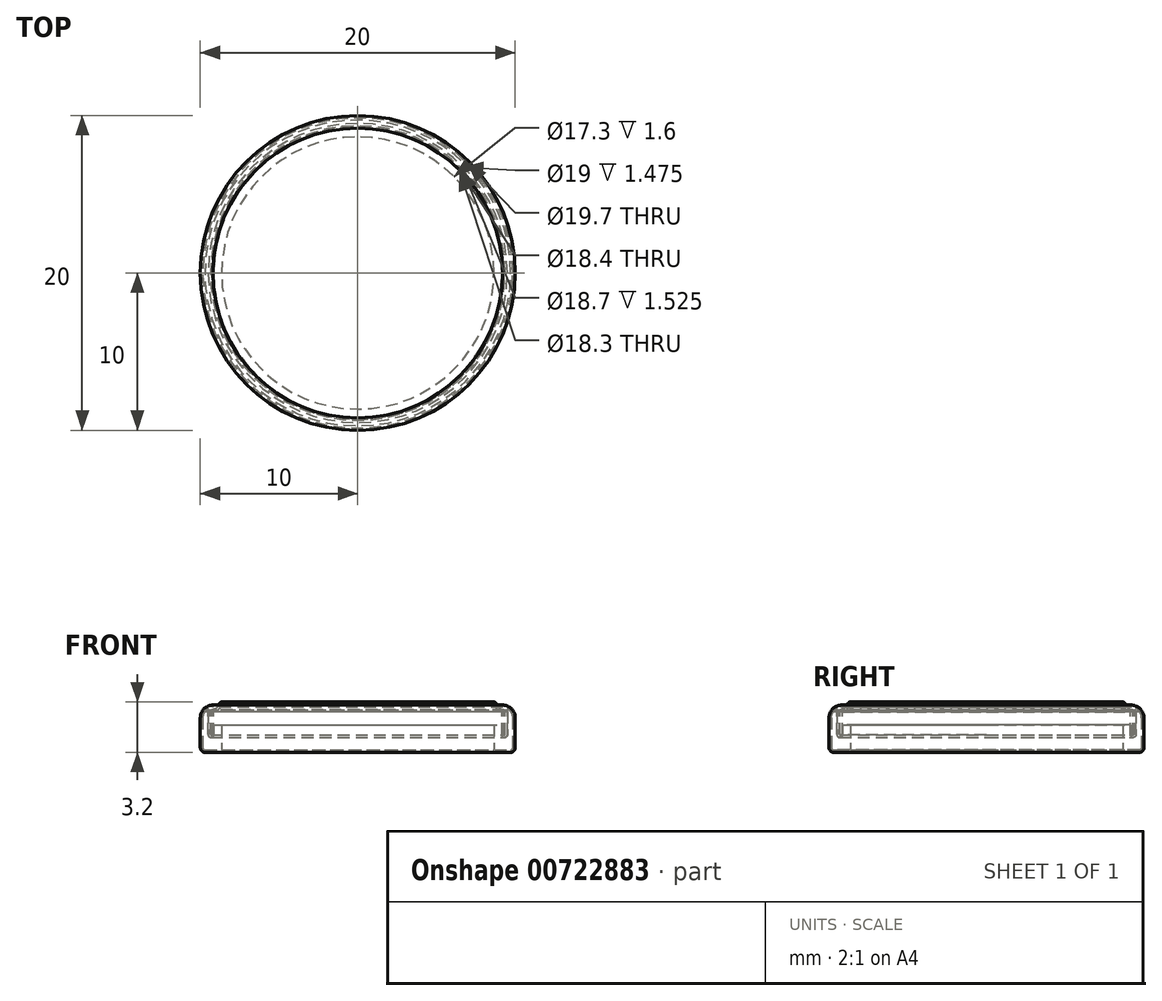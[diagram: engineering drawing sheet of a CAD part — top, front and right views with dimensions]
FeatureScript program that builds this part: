
annotation { "Feature Type Name" : "Feature", "Feature Type Description" : "" }
export const myFeature = defineFeature(function(context is Context, id is Id, definition is map)
    precondition{}
    {
        {
            var Q0;
            Q0=qCreatedBy(makeId("Front.planeOp"),FACE);
            var sketch = newSketch(context, id + "F0", { "sketchPlane" : qUnion([Q0])});
            skLineSegment(sketch, "E0", {"start": v(0, 8.39) * mm, "end": v(0, 0) * mm, "construction": true});
            skLineSegment(sketch, "E1", {"start": v(0, 0) * mm, "end": v(-9.7, 0) * mm});
            skLineSegment(sketch, "E2", {"start": v(-10, 0.3) * mm, "end": v(-10, 2.2) * mm});
            skArc(sketch, "E3", {"start": v(-9.2, 3) * mm, "mid": v(-9.77, 2.77) * mm, "end": v(-10, 2.2) * mm});
            skLineSegment(sketch, "E4", {"start": v(-8.63, 3.2) * mm, "end": v(0, 3.2) * mm});
            skArc(sketch, "E5", {"start": v(-9.3, 2.7) * mm, "mid": v(-9, 2.8) * mm, "end": v(-8.82, 3.06) * mm});
            skLineSegment(sketch, "E6", {"start": v(-8.8, 3.2) * mm, "end": v(-8.8, 9.73) * mm, "construction": true});
            skLineSegment(sketch, "E7", {"start": v(-9.2, 3) * mm, "end": v(-7.95, 3) * mm, "construction": true});
            skLineSegment(sketch, "E8", {"start": v(-9.3, 2.7) * mm, "end": v(-10.43, 2.7) * mm, "construction": true});
            skLineSegment(sketch, "E9.0", {"start": v(0, 0.15) * mm, "end": v(-9.7, 0.15) * mm});
            skLineSegment(sketch, "E9.1", {"start": v(-9.85, 0.3) * mm, "end": v(-9.85, 2.2) * mm});
            skArc(sketch, "E9.2", {"start": v(-9.2, 2.85) * mm, "mid": v(-9.66, 2.66) * mm, "end": v(-9.85, 2.2) * mm});
            skLineSegment(sketch, "E10", {"start": v(-9.2, 3) * mm, "end": v(-9.2, 2.85) * mm});
            skLineSegment(sketch, "E11", {"start": v(-9.3, 2.7) * mm, "end": v(-9.3, 1.12) * mm});
            skArc(sketch, "E12", {"start": v(-9.35, 1.12) * mm, "mid": v(-9.32, 1.1) * mm, "end": v(-9.3, 1.12) * mm});
            skLineSegment(sketch, "E13", {"start": v(-9.35, 1.12) * mm, "end": v(-9.35, 2.65) * mm});
            skLineSegment(sketch, "E14.0", {"start": v(-9.5, 1.12) * mm, "end": v(-9.5, 2.65) * mm});
            skArc(sketch, "E14.1", {"start": v(-9.5, 1.12) * mm, "mid": v(-9.32, 0.95) * mm, "end": v(-9.15, 1.12) * mm});
            skLineSegment(sketch, "E14.2", {"start": v(-9.15, 2.57) * mm, "end": v(-9.15, 1.12) * mm});
            skArc(sketch, "E14.3", {"start": v(-9.15, 2.57) * mm, "mid": v(-8.85, 2.73) * mm, "end": v(-8.68, 3.01) * mm});
            skLineSegment(sketch, "E15", {"start": v(-9.5, 2.65) * mm, "end": v(-9.35, 2.65) * mm});
            skLineSegment(sketch, "E16", {"start": v(-8.63, 3.05) * mm, "end": v(0, 3.05) * mm});
            skLineSegment(sketch, "E17", {"start": v(0, 0.15) * mm, "end": v(0, 0) * mm});
            skLineSegment(sketch, "E18", {"start": v(0, 3.2) * mm, "end": v(0, 3.05) * mm});
            skPoint(sketch, "E19.visualSharp", {"position": v(-9.85, 0.15) * mm});
            skArc(sketch, "E19.filletArc", {"start": v(-9.85, 0.3) * mm, "mid": v(-9.8, 0.2) * mm, "end": v(-9.7, 0.15) * mm});
            skPoint(sketch, "E20.visualSharp", {"position": v(-10, 0) * mm});
            skArc(sketch, "E20.filletArc", {"start": v(-10, 0.3) * mm, "mid": v(-9.91, 0.09) * mm, "end": v(-9.7, 0) * mm});
            skPoint(sketch, "E21.visualSharp", {"position": v(-8.8, 3.2) * mm});
            skArc(sketch, "E21.filletArc", {"start": v(-8.63, 3.2) * mm, "mid": v(-8.75, 3.16) * mm, "end": v(-8.82, 3.06) * mm});
            skPoint(sketch, "E22.visualSharp", {"position": v(-8.67, 3.05) * mm});
            skArc(sketch, "E22.filletArc", {"start": v(-8.63, 3.05) * mm, "mid": v(-8.66, 3.04) * mm, "end": v(-8.68, 3.01) * mm});
            skSolve(sketch);
        }
        {
            var Q0;
            Q0 = qSketchRegion(id + "F0", true);
            var Q1;
            Q1=sQuery(id+"F0.wireOp",EDGE,"E0");
            revolve(context, id + "F1", {"surfaceOperationType" : NewSurfaceOperationType.NEW, "entities" : qUnion([Q0]), "axis" : qUnion([Q1]), "revolveType" : RevolveType.FULL});
        }
        {
            var Q0;
            Q0=qCreatedBy(makeId("Front.planeOp"),FACE);
            var sketch = newSketch(context, id + "F2", { "sketchPlane" : qUnion([Q0])});
            skLineSegment(sketch, "E23.0", {"start": v(-9.85, 0.3) * mm, "end": v(-9.85, 2.2) * mm});
            skArc(sketch, "E23.1", {"start": v(-9.85, 0.3) * mm, "mid": v(-9.8, 0.2) * mm, "end": v(-9.7, 0.15) * mm});
            skLineSegment(sketch, "E23.2", {"start": v(-8.65, 0.15) * mm, "end": v(-9.7, 0.15) * mm});
            skLineSegment(sketch, "E24", {"start": v(-8.65, 1.75) * mm, "end": v(-8.65, 0.15) * mm});
            skLineSegment(sketch, "E25", {"start": v(-8.65, 1.75) * mm, "end": v(-9.15, 1.75) * mm});
            skLineSegment(sketch, "E26.0", {"start": v(-9.15, 1.75) * mm, "end": v(-9.15, 1.12) * mm});
            skArc(sketch, "E26.1", {"start": v(-9.5, 1.12) * mm, "mid": v(-9.32, 0.95) * mm, "end": v(-9.15, 1.12) * mm});
            skLineSegment(sketch, "E26.2", {"start": v(-9.5, 1.12) * mm, "end": v(-9.5, 2.6) * mm});
            skLineSegment(sketch, "E27", {"start": v(-9.71, 2.6) * mm, "end": v(-9.5, 2.6) * mm});
            skPoint(sketch, "E28.orphan", {"position": v(-9.85, 2.2) * mm});
            skArc(sketch, "E29.0", {"start": v(-9.71, 2.6) * mm, "mid": v(-9.81, 2.41) * mm, "end": v(-9.85, 2.2) * mm});
            skLineSegment(sketch, "E30", {"start": v(0, 0) * mm, "end": v(0, 5.68) * mm, "construction": true});
            skSolve(sketch);
        }
        {
            var Q0;
            Q0 = qSketchRegion(id + "F2", true);
            var Q1;
            Q1=sQuery(id+"F2.wireOp",EDGE,"E30");
            revolve(context, id + "F3", {"surfaceOperationType" : NewSurfaceOperationType.NEW, "entities" : qUnion([Q0]), "axis" : qUnion([Q1]), "revolveType" : RevolveType.FULL});
        }
    });
